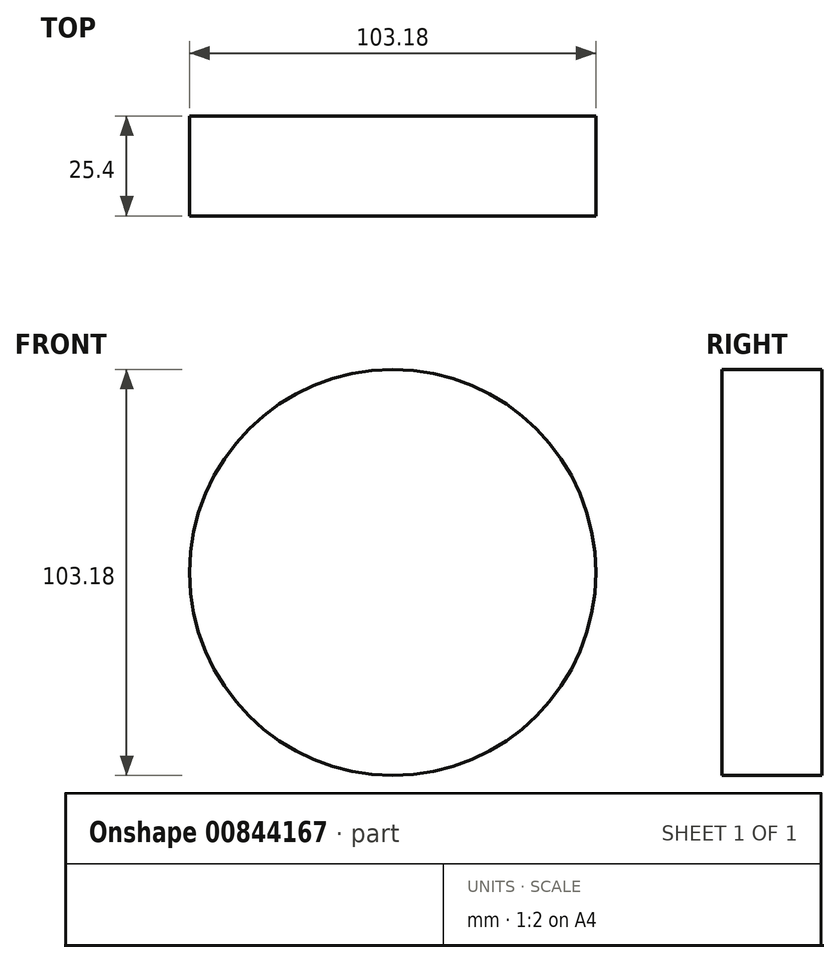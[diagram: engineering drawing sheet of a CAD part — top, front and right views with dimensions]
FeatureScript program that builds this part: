
annotation { "Feature Type Name" : "Feature", "Feature Type Description" : "" }
export const myFeature = defineFeature(function(context is Context, id is Id, definition is map)
    precondition{}
    {
        {
            var Q0;
            Q0=qCreatedBy(makeId("Front.planeOp"),FACE);
            var sketch = newSketch(context, id + "F0", { "sketchPlane" : qUnion([Q0])});
            skCircle(sketch, "E0", {"center": v(0, 0) * mm, "radius": 51.6 * mm});
            skSolve(sketch);
        }
        {
            var Q0;
            Q0=makeQuery(id+"F0.imprint","IMPRINT",FACE,{"disambiguationData":[TD([[makeQuery(id+"F0.imprint","IMPRINT",EDGE,{"derivedFrom":sQuery(id+"F0.wireOp",EDGE,"E0")}),1.0]])]});
            extrude(context, id + "F1", {"entities" : qUnion([Q0]), "oppositeDirection" : true, "depth" : 25.4 * mm, "offsetDistance" : 25.4 * mm});
        }
    });
